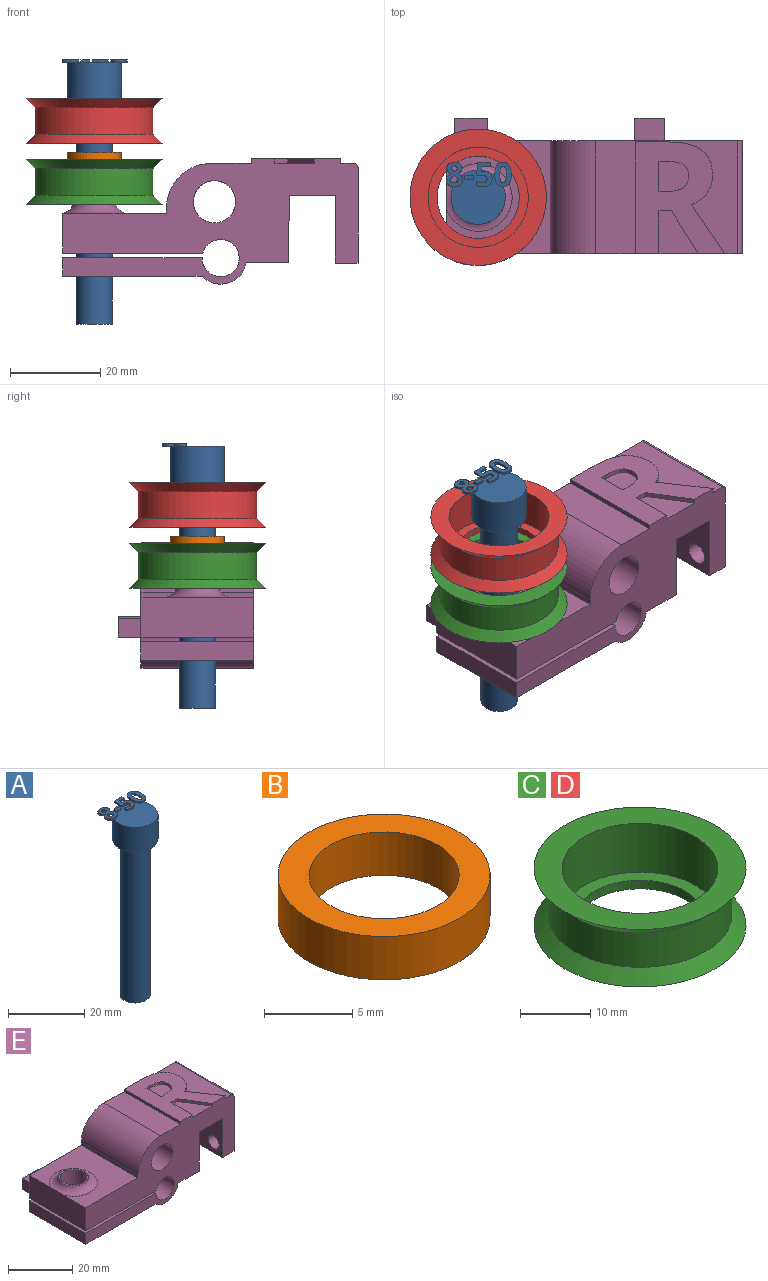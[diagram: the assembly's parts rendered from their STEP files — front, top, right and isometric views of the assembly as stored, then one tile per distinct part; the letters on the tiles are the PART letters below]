
ASSEMBLY  parts=5 mates=4
PART A: 86 faces, bbox 14.5x13.7x58.5 mm
  f0: plane 12x12mm, normal (0,0,1), area 99.4mm2, adj f5,f22,f23,f24,f25,f26,f40,f41
  f1: plane 1x0.26mm, normal (0,0,1), area 0.1mm2, adj f5,f46,f47,f48,f49
  f2: plane 0.85x0.68mm, normal (0,0,1), area 0.2mm2, adj f5,f29,f30,f31
  f3: cylinder r=4mm len=50mm, axis (0,0,-1), area 1256.6mm2, adj f4,f6
  f4: plane 8x8mm, normal (0,0,-1), area 50.3mm2, adj f3
  f5: cylinder r=6mm len=12mm, axis (0,0,-1), area 301.6mm2, adj f0,f1,f2,f6,f39,f45,f67,f85
  f6: plane 12x12mm, normal (0,0,-1), area 62.8mm2, adj f3,f5
  f7: extruded ~0.5x0.46mm, area 0.2mm2, adj f8,f37,f38,f39
  f8: extruded ~0.5x0.46mm, area 0.2mm2, adj f7,f9,f38,f39
  f9: extruded ~0.5x0.39mm, area 0.2mm2, adj f8,f10,f38,f39
  f10: extruded ~0.5x0.4mm, area 0.2mm2, adj f9,f11,f38,f39
  f11: extruded ~0.5x0.49mm, area 0.3mm2, adj f10,f12,f38,f39
  f12: extruded ~0.5x0.5mm, area 0.3mm2, adj f11,f13,f38,f39
  f13: extruded ~0.5x0.39mm, area 0.2mm2, adj f12,f37,f38,f39
  f14: extruded ~1.22x0.5mm, area 0.6mm2, adj f15,f35,f38,f39
  f15: extruded ~1.22x0.5mm, area 0.6mm2, adj f14,f16,f38,f39
  f16: extruded ~0.91x0.5mm, area 0.5mm2, adj f15,f17,f38,f39
  f17: extruded ~0.71x0.5mm, area 0.4mm2, adj f16,f18,f38,f39
  f18: extruded ~0.65x0.61mm, area 0.4mm2, adj f17,f19,f38,f39
  f19: extruded ~0.77x0.62mm, area 0.5mm2, adj f18,f20,f38,f39
  f20: extruded ~0.8x0.5mm, area 0.4mm2, adj f19,f21,f38,f39
  f21: extruded ~1.04x0.5mm, area 0.6mm2, adj f20,f22,f38,f39
  f22: extruded ~1.36x0.5mm, area 0.7mm2, adj f0,f21,f23,f38,f39
  f23: extruded ~1.33x0.5mm, area 0.7mm2, adj f0,f22,f24,f38
  f24: extruded ~1.04x0.51mm, area 0.6mm2, adj f0,f23,f25,f38
  f25: extruded ~0.75x0.5mm, area 0.4mm2, adj f0,f24,f26,f38
  f26: extruded ~0.85x0.66mm, area 0.5mm2, adj f0,f25,f27,f38,f39
  f27: extruded ~0.72x0.56mm, area 0.5mm2, adj f26,f28,f38,f39
  f28: extruded ~0.72x0.5mm, area 0.4mm2, adj f27,f35,f38,f39
  f29: extruded ~0.5x0.45mm, area 0.3mm2, adj f2,f30,f36,f38,f39
  f30: extruded ~0.5x0.47mm, area 0.3mm2, adj f2,f29,f31,f38
  f31: extruded ~0.62x0.5mm, area 0.3mm2, adj f2,f30,f32,f38,f39
  f32: extruded ~0.59x0.5mm, area 0.3mm2, adj f31,f33,f38,f39
  f33: extruded ~0.5x0.48mm, area 0.3mm2, adj f32,f34,f38,f39
  f34: extruded ~0.89x0.77mm, area 0.6mm2, adj f33,f36,f38,f39
  f35: extruded ~0.93x0.5mm, area 0.5mm2, adj f14,f28,f38,f39
  f36: extruded ~0.66x0.5mm, area 0.4mm2, adj f29,f34,f38,f39
  f37: extruded ~0.5x0.39mm, area 0.2mm2, adj f7,f13,f38,f39
  f38: plane 5.4x3.69mm, normal (0,0,1), area 12.7mm2, adj f7,f8,f9,f10,f11,f12,f13,f14
  f39: plane 5.4x3.53mm, normal (0,0,-1), area 10.2mm2, adj f5,f7,f8,f9,f10,f11,f12,f13
  f40: plane 0.9x0.5mm, normal (-1,0,0), area 0.4mm2, adj f0,f41,f43,f44
  f41: plane 1.93x0.5mm, normal (0,-1,0), area 1mm2, adj f0,f40,f42,f44
  f42: plane 0.9x0.5mm, normal (1,0,0), area 0.4mm2, adj f0,f41,f43,f44
  f43: plane 1.93x0.5mm, normal (0,1,0), area 1mm2, adj f0,f40,f42,f44
  f44: plane 1.93x0.9mm, normal (0,0,1), area 1.7mm2, adj f40,f41,f42,f43
  f45: plane 0.76x0.31mm, normal (0,0,-1), area 0mm2, adj f5,f46
  f46: extruded ~1.21x0.5mm, area 0.7mm2, adj f0,f1,f45,f47,f65,f66
  f47: extruded ~0.54x0.5mm, area 0.3mm2, adj f1,f46,f48,f66
  f48: plane 0.5x0.13mm, normal (-0.2,0.98,0), area 0.1mm2, adj f1,f47,f49,f66
  f49: plane 1.03x0.5mm, normal (1,-0.09,0), area 0.5mm2, adj f1,f48,f50,f66,f67
  f50: plane 1.88x0.5mm, normal (0,-1,0), area 0.9mm2, adj f49,f51,f66,f67
  f51: plane 0.94x0.5mm, normal (1,0,0), area 0.5mm2, adj f50,f52,f66,f67
  f52: plane 2.85x0.5mm, normal (0,1,0), area 1.4mm2, adj f51,f53,f66,f67
  f53: plane 2.68x0.5mm, normal (-1,0.07,0), area 1.3mm2, adj f0,f52,f54,f66,f67
  f54: plane 0.5x0.44mm, normal (-0.47,-0.88,0), area 0.3mm2, adj f0,f53,f55,f66
  f55: extruded ~0.5x0.37mm, area 0.2mm2, adj f0,f54,f56,f66
  f56: extruded ~0.5x0.42mm, area 0.2mm2, adj f0,f55,f57,f66
  f57: extruded ~1.05x0.8mm, area 0.8mm2, adj f0,f56,f58,f66
  f58: extruded ~1.02x0.83mm, area 0.8mm2, adj f0,f57,f59,f66
  f59: extruded ~0.72x0.5mm, area 0.4mm2, adj f0,f58,f60,f66
  f60: extruded ~0.66x0.5mm, area 0.4mm2, adj f0,f59,f61,f66
  f61: plane 0.96x0.5mm, normal (-1,0,0), area 0.5mm2, adj f0,f60,f62,f66
  f62: extruded ~1.42x0.5mm, area 0.7mm2, adj f0,f61,f63,f66
  f63: extruded ~1.55x0.5mm, area 0.8mm2, adj f0,f62,f64,f66
  f64: extruded ~1.36x0.54mm, area 0.8mm2, adj f0,f63,f65,f66
  f65: extruded ~1.17x0.5mm, area 0.6mm2, adj f0,f46,f64,f66
  f66: plane 5.33x3.51mm, normal (0,0,1), area 10.9mm2, adj f46,f47,f48,f49,f50,f51,f52,f53
  f67: plane 2.97x1.71mm, normal (0,0,-1), area 3.5mm2, adj f5,f49,f50,f51,f52,f53
  f68: extruded ~1.39x0.5mm, area 0.7mm2, adj f69,f83,f84,f85
  f69: extruded ~1.39x0.5mm, area 0.7mm2, adj f68,f70,f84,f85
  f70: extruded ~0.56x0.5mm, area 0.4mm2, adj f69,f71,f84,f85
  f71: extruded ~0.56x0.5mm, area 0.4mm2, adj f70,f72,f84,f85
  f72: extruded ~1.39x0.5mm, area 0.7mm2, adj f71,f73,f84,f85
  f73: extruded ~1.38x0.5mm, area 0.7mm2, adj f72,f74,f84,f85
  f74: extruded ~0.56x0.5mm, area 0.4mm2, adj f73,f83,f84,f85
  f75: extruded ~2.04x0.5mm, area 1.1mm2, adj f76,f82,f84,f85
  f76: extruded ~2.02x0.5mm, area 1.1mm2, adj f75,f77,f84,f85
  f77: extruded ~1.38x0.69mm, area 0.8mm2, adj f76,f78,f84,f85
  f78: extruded ~1.38x0.66mm, area 0.8mm2, adj f77,f79,f84,f85
  f79: extruded ~2.05x0.5mm, area 1.1mm2, adj f78,f80,f84,f85
  f80: extruded ~2.02x0.5mm, area 1mm2, adj f0,f79,f81,f84,f85
  f81: extruded ~1.37x0.68mm, area 0.8mm2, adj f0,f80,f82,f84
  f82: extruded ~1.39x0.66mm, area 0.8mm2, adj f0,f75,f81,f84,f85
  f83: extruded ~0.56x0.5mm, area 0.4mm2, adj f68,f74,f84,f85
  f84: plane 5.41x3.68mm, normal (0,0,1), area 12.1mm2, adj f68,f69,f70,f71,f72,f73,f74,f75
  f85: plane 5.41x3.68mm, normal (0,0,-1), area 10.3mm2, adj f5,f68,f69,f70,f71,f72,f73,f74
PART B: 4 faces, bbox 12x12x3 mm
  f0: cylinder r=4.25mm len=8.5mm, axis (0,0,-1), area 80.1mm2, adj f2,f3
  f1: cylinder r=6mm len=12mm, axis (0,0,-1), area 113.1mm2, adj f2,f3
  f2: plane 12x12mm, normal (0,0,1), area 56.4mm2, adj f0,f1
  f3: plane 12x12mm, normal (0,0,-1), area 56.4mm2, adj f0,f1
PART C: 8 faces, bbox 30.2x30.2x10 mm
  f0: plane 30.2x30.2mm, normal (0,0,1), area 329.2mm2, adj f1,f7
  f1: cylinder r=11.1mm len=22.2mm, axis (0,0,-1), area 592.8mm2, adj f0,f2
  f2: plane 22.2x22.2mm, normal (0,0,1), area 126.9mm2, adj f1,f3
  f3: cylinder r=9.1mm len=18.2mm, axis (0,0,-1), area 85.8mm2, adj f2,f4
  f4: plane 30.2x30.2mm, normal (0,0,-1), area 456.2mm2, adj f3,f5
  f5: cone r=13.1mm half-angle=45deg, axis (0,0,-1), area 250.6mm2, adj f4,f6
  f6: cylinder r=13.1mm len=26.2mm, axis (0,0,-1), area 493.9mm2, adj f5,f7
  f7: cone r=15.1mm half-angle=45deg, axis (0,0,1), area 250.6mm2, adj f0,f6
PART D: same geometry as C
PART E: 56 faces, bbox 68.9x30x27.7 mm
  f0: plane 31.42x25mm, normal (0,0,1), area 392.1mm2, adj f14,f15,f25,f27,f40,f41,f42,f43
  f1: plane 9.51x8.71mm, normal (0,0,1), area 54.7mm2, adj f14,f37,f38,f39
  f2: plane 25x4.12mm, normal (-1,0,0), area 103mm2, adj f5,f14,f15,f19
  f3: cylinder r=4.17mm len=8.35mm, axis (0,0,1), area 108.1mm2, adj f5,f19
  f4: plane 25x9.34mm, normal (0,0,-1), area 233.4mm2, adj f13,f14,f15,f17
  f5: plane 30.88x25mm, normal (0,0,-1), area 717.2mm2, adj f2,f3,f14,f15,f17
  f6: plane 25x8.82mm, normal (-1,0,0), area 219.6mm2, adj f7,f14,f15,f20,f24
  f7: plane 25x23mm, normal (0,0,1), area 400mm2, adj f6,f8,f14,f15,f24
  f8: plane 25x1.1mm, normal (-1,0,0), area 27.5mm2, adj f7,f14,f15,f25
  f9: plane 25x21.09mm, normal (1,0,0), area 493.5mm2, adj f10,f14,f15,f22,f23,f27
  f10: plane 25x5mm, normal (0,0,-1), area 125mm2, adj f9,f11,f14,f15
  f11: plane 25x15mm, normal (-1,0,0), area 341.3mm2, adj f10,f12,f14,f15,f22,f23
  f12: plane 25x10.2mm, normal (0,0,-1), area 255mm2, adj f11,f13,f14,f15
  f13: plane 25x14.91mm, normal (1,0,-0.01), area 372.8mm2, adj f4,f12,f14,f15
  f14: plane 65.42x27.75mm, normal (0,-1,0), area 997.9mm2, adj f0,f1,f2,f4,f5,f6,f7,f8
  f15: plane 65.42x26.75mm, normal (0,1,0), area 926.8mm2, adj f0,f2,f4,f5,f6,f7,f8,f9
  f16: cylinder r=4.17mm len=10.78mm, axis (0,0,1), area 282.8mm2, adj f20,f21
  f17: cylinder r=5.75mm len=25mm, axis (0,-1,0), area 315.9mm2, adj f4,f5,f14,f15
  f18: cylinder r=4.1mm len=25mm, axis (0,-1,0), area 618.7mm2, adj f14,f15,f19,f20
  f19: plane 30.91x25mm, normal (0,0,1), area 718.1mm2, adj f2,f3,f14,f15,f18
  f20: plane 31.07x30mm, normal (0,0,-1), area 758.4mm2, adj f6,f14,f15,f16,f18,f29,f30,f31
  f21: plane 9.35x9.35mm, normal (0,0,1), area 13.9mm2, adj f16,f24
  f22: cylinder r=2.43mm len=5mm, axis (1,0,0), area 76.2mm2, adj f9,f11
  f23: cylinder r=2.2mm len=5mm, axis (1,0,0), area 69.1mm2, adj f9,f11
  f24: torus R=7.5mm, axis (0,0,-1), area 134.6mm2, adj f6,f7,f21
  f25: cylinder r=10mm len=25mm, axis (0,-1,0), area 392.7mm2, adj f0,f8,f14,f15
  f26: cylinder r=4.68mm len=25mm, axis (0,-1,0), area 735.2mm2, adj f14,f15
  f27: cylinder r=1mm len=25mm, axis (0,-1,0), area 39.3mm2, adj f0,f9,f14,f15
  f28: plane 7.3x5mm, normal (0,0,1), area 36.5mm2, adj f15,f29,f30,f31
  f29: plane 5x4.12mm, normal (-1,0,0), area 20.6mm2, adj f15,f20,f28,f31
  f30: plane 5x4.12mm, normal (1,0,0), area 20.6mm2, adj f15,f20,f28,f31
  f31: plane 7.3x4.12mm, normal (0,1,0), area 30.1mm2, adj f20,f28,f29,f30
  f32: plane 6.63x5mm, normal (0,0,1), area 33.2mm2, adj f15,f33,f35,f36
  f33: plane 5x4.5mm, normal (-1,0,0), area 22.5mm2, adj f15,f32,f34,f36
  f34: plane 6.63x5mm, normal (0,0,-1), area 33.2mm2, adj f15,f33,f35,f36
  f35: plane 5x4.5mm, normal (1,0,0), area 22.5mm2, adj f15,f32,f34,f36
  f36: plane 6.63x4.5mm, normal (0,1,0), area 29.9mm2, adj f32,f33,f34,f35
  f37: plane 9.51x1mm, normal (1,0,0), area 9.5mm2, adj f1,f14,f38,f54
  f38: plane 2.79x1mm, normal (0,-1,0), area 2.8mm2, adj f1,f37,f39,f54
  f39: plane 9.51x5.92mm, normal (-0.85,-0.53,0), area 11.2mm2, adj f1,f14,f38,f54
  f40: extruded ~10.8x7.29mm, area 13mm2, adj f0,f14,f41,f54
  f41: extruded ~3.41x2.67mm, area 4.4mm2, adj f0,f40,f42,f54
  f42: extruded ~3.89x1.2mm, area 4.1mm2, adj f0,f41,f43,f54
  f43: extruded ~5.59x2.42mm, area 6.3mm2, adj f0,f42,f44,f54
  f44: extruded ~7.48x1.84mm, area 7.8mm2, adj f0,f43,f45,f54
  f45: plane 7.22x1mm, normal (0,1,0), area 7.2mm2, adj f0,f44,f46,f54
  f46: plane 24.79x1mm, normal (-1,0,0), area 24.8mm2, adj f0,f14,f45,f54
  f47: plane 1.69x1mm, normal (0,1,0), area 1.7mm2, adj f48,f53,f54,f55
  f48: plane 6.7x1mm, normal (1,0,0), area 6.7mm2, adj f47,f49,f54,f55
  f49: plane 1.6x1mm, normal (0,-1,0), area 1.6mm2, adj f48,f50,f54,f55
  f50: extruded ~3.75x1mm, area 3.9mm2, adj f49,f51,f54,f55
  f51: extruded ~2.51x1.21mm, area 2.9mm2, adj f50,f52,f54,f55
  f52: extruded ~2.61x1.19mm, area 3mm2, adj f51,f53,f54,f55
  f53: extruded ~3.68x1mm, area 3.8mm2, adj f47,f52,f54,f55
  f54: plane 24.79x19.8mm, normal (0,0,1), area 300mm2, adj f14,f37,f38,f39,f40,f41,f42,f43
  f55: plane 6.7x6.56mm, normal (0,0,1), area 38.8mm2, adj f47,f48,f49,f50,f51,f52,f53
PLACE A t=(-103.78,-12.5,-13.6)mm
PLACE B rot(axis=(1,0,0),180deg) t=(-103.78,-12.5,24.4)mm
PLACE C t=(-103.78,-12.5,18.1)mm
PLACE D t=(-103.78,-12.5,31.6)mm
PLACE E at identity
MATE fastened A.f3 <-> D.f1  axis (0,0,-1) through (-103.78,-12.5,36.4)mm
MATE fastened B.f0 <-> C.f1  axis (0,0,1) through (-103.78,-12.5,21.4)mm
MATE fastened C.f1 <-> E.f3  axis (0,0,-1) through (-103.78,-12.5,12.9)mm
MATE fastened D.f1 <-> B.f0  axis (0,0,-1) through (-103.78,-12.5,26.4)mm
